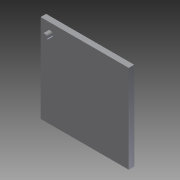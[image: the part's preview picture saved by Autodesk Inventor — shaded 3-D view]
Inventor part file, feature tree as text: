
AUTODESK INVENTOR PART (.ipt)
format: ipt  version: 2011 (Build 150239000, 239)  size: 91,136 bytes
history: native  units: in
note: dims shown in document units (in); Inventor stores cm internally (conversion verified against a paired STEP export)
features: extrude x4, sketch x4
ambient origin geometry x8: Origin, YZ Plane, XZ Plane, XY Plane, X Axis, Y Axis, Z Axis, Center Point
bodies: Solid1 (feature_tree)
feature tree (8):
  extrude  "Extrusion1"  Depth=4.0in
  extrude  "Extrusion2"  Depth=2.0in
  extrude  "Extrusion3"  Depth=1.0in
  extrude  "Extrusion4"  Depth=2.0in
  sketch  "Sketch1"  dims[d0=4.0in d1=4.0in]
  sketch  "Sketch2"  dims[d2=0.25in d3=0.0in d4=2.0in]
  sketch  "Sketch3"  dims[d5=2.0in d6=1.0in]
  sketch  "Sketch4"  dims[d7=0.25in d8=0.0in d9=2.0in d10=1.5655in d11=0.435in d12=0.25in d13=0.25in d14=0.0in d15=0.75in d16=0.0in]
